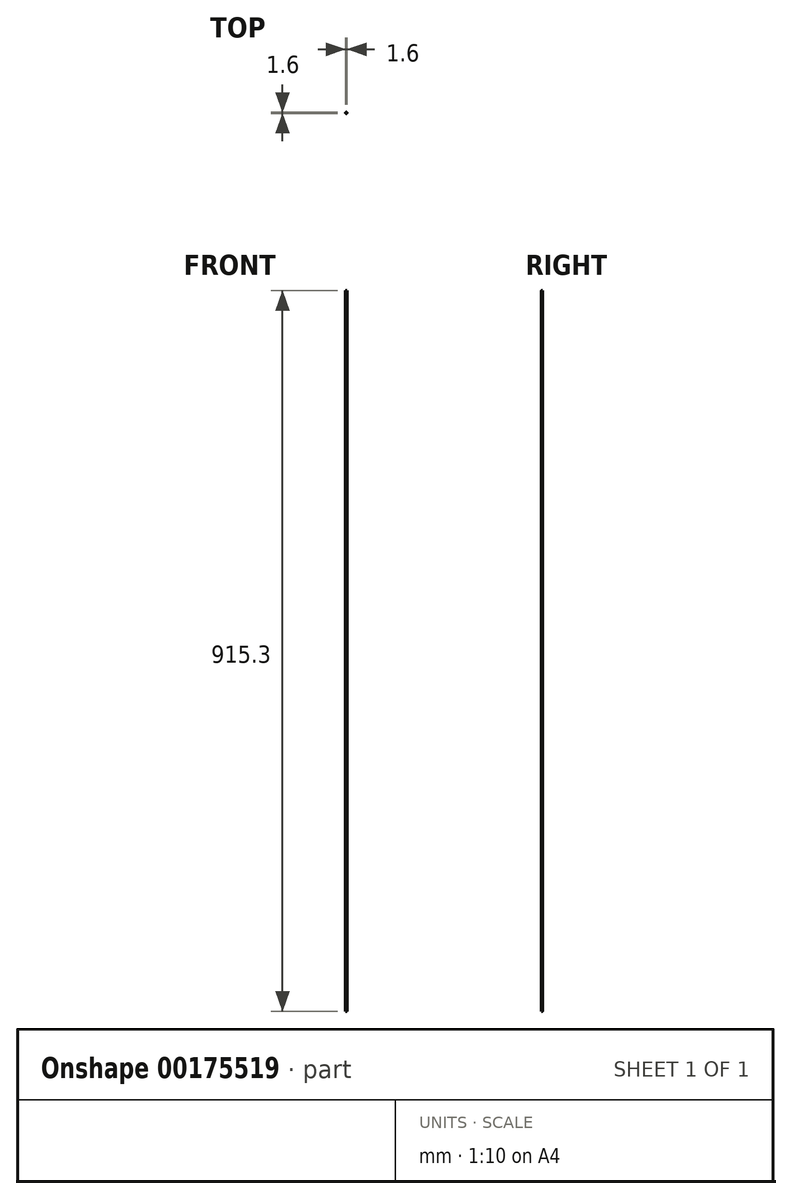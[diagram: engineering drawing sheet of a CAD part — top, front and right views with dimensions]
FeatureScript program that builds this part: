
annotation { "Feature Type Name" : "Feature", "Feature Type Description" : "" }
export const myFeature = defineFeature(function(context is Context, id is Id, definition is map)
    precondition{}
    {
        {
            var Q0;
            Q0=qCreatedBy(makeId("Top.planeOp"),FACE);
            var sketch = newSketch(context, id + "F0", { "sketchPlane" : qUnion([Q0])});
            skCircle(sketch, "E0", {"center": v(0, 0) * mm, "radius": 0.8 * mm});
            skSolve(sketch);
        }
        {
            var Q0;
            Q0=qSketchRegion(id+"F0",true);
            extrude(context, id + "F1", {"entities" : qUnion([Q0]), "depth" : 915.3 * mm});
        }
    });
